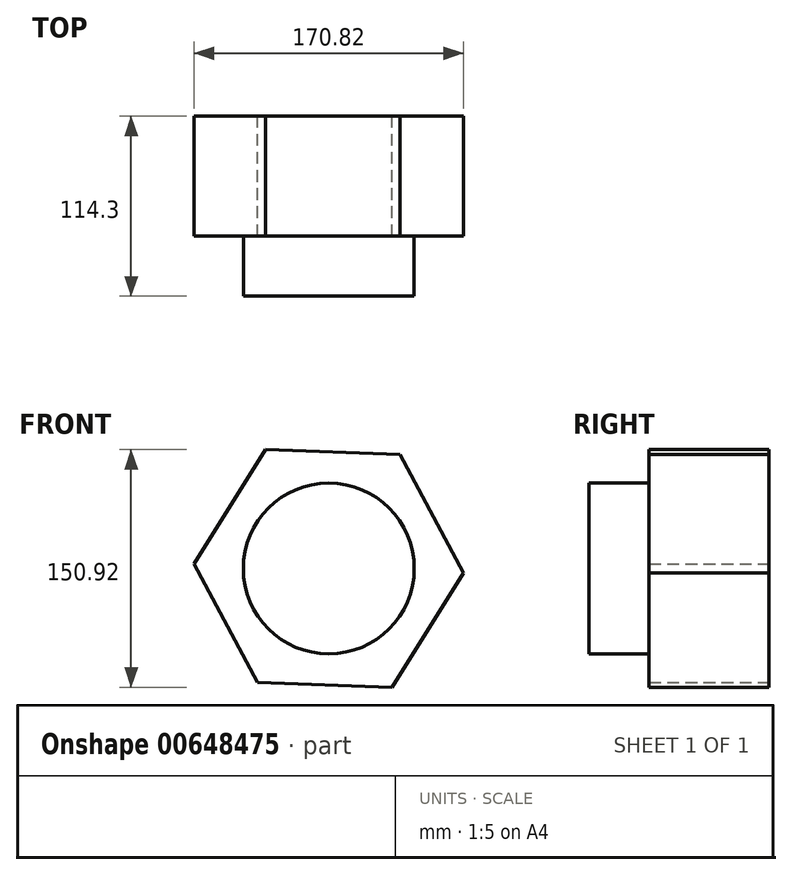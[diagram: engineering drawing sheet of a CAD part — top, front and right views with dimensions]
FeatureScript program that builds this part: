
annotation { "Feature Type Name" : "Feature", "Feature Type Description" : "" }
export const myFeature = defineFeature(function(context is Context, id is Id, definition is map)
    precondition{}
    {
        {
            var Q0;
            Q0=qCreatedBy(makeId("Front.planeOp"),FACE);
            var sketch = newSketch(context, id + "F0", { "sketchPlane" : qUnion([Q0])});
            skCircle(sketch, "E0.cCircle", {"center": v(0, 0) * mm, "radius": 74.01 * mm, "construction": true});
            skLineSegment(sketch, "E0.0", {"start": v(-45.29, -72.48) * mm, "end": v(-85.41, 2.98) * mm});
            skLineSegment(sketch, "E0.1", {"start": v(-85.41, 2.98) * mm, "end": v(-40.12, 75.46) * mm});
            skLineSegment(sketch, "E0.2", {"start": v(-40.12, 75.46) * mm, "end": v(45.29, 72.48) * mm});
            skLineSegment(sketch, "E0.3", {"start": v(45.29, 72.48) * mm, "end": v(85.41, -2.98) * mm});
            skLineSegment(sketch, "E0.4", {"start": v(85.41, -2.98) * mm, "end": v(40.12, -75.46) * mm});
            skLineSegment(sketch, "E0.5", {"start": v(40.12, -75.46) * mm, "end": v(-45.29, -72.48) * mm});
            skPoint(sketch, "E0.0.midPoint", {"position": v(-65.35, -34.75) * mm});
            skSolve(sketch);
        }
        {
            var Q0;
            Q0=makeQuery(id+"F0.imprint","IMPRINT",FACE,{"disambiguationData":[TD([[makeQuery(id+"F0.imprint","IMPRINT",EDGE,{"derivedFrom":sQuery(id+"F0.wireOp",EDGE,"E0.0")}),-1.0]])]});
            extrude(context, id + "F1", {"entities" : qUnion([Q0]), "depth" : 76.2 * mm, "offsetDistance" : 25.4 * mm});
        }
        {
            var Q0;
            Q0=makeQuery(id+"F1.opExtrude","CAP_FACE",FACE,{"disambiguationData":[OSD([sQuery(id+"F0.wireOp",EDGE,"E0.0"),sQuery(id+"F0.wireOp",EDGE,"E0.1"),sQuery(id+"F0.wireOp",EDGE,"E0.2"),sQuery(id+"F0.wireOp",EDGE,"E0.3"),sQuery(id+"F0.wireOp",EDGE,"E0.4"),sQuery(id+"F0.wireOp",EDGE,"E0.5")])],"isStart":false});
            var sketch = newSketch(context, id + "F2", { "sketchPlane" : qUnion([Q0])});
            skCircle(sketch, "E1", {"center": v(0, 0) * mm, "radius": 54.27 * mm});
            skSolve(sketch);
        }
        {
            var Q0;
            Q0 = qSketchRegion(id + "F2", true);
            extrude(context, id + "F3", {"entities" : qUnion([Q0]), "operationType" : NewBodyOperationType.ADD, "depth" : 38.1 * mm, "offsetDistance" : 25.4 * mm});
        }
    });
